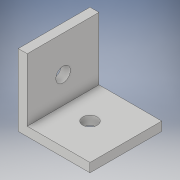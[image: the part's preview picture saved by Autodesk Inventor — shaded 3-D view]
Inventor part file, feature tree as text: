
AUTODESK INVENTOR PART (.ipt)
format: ipt  version: 2018 (Build 220112000, 112)  size: 116,224 bytes
history: native  units: in
note: dims shown in document units (in); Inventor stores cm internally (conversion verified against a paired STEP export)
features: extrude x3, sketch x3
ambient origin geometry x8: Origin, YZ Plane, XZ Plane, XY Plane, X Axis, Y Axis, Z Axis, Center Point
bodies: Solid1 (feature_tree)
feature tree (6):
  extrude  "Extrusion1"  Depth=1.0in
  extrude  "Extrusion2"  Depth=0.125in
  extrude  "Extrusion3"  Depth=1.0in
  sketch  "Sketch1"  dims[d0=0.125in d1=1.0in]
  sketch  "Sketch2"  dims[d2=1.0in d3=0.125in]
  sketch  "Sketch3"  dims[d4=1.0in d5=0.0in d6=0.5in d7=90.0deg d8=0.2031in d9=1.0in d10=0.0in d11=0.5in d12=180.0deg d13=0.2031in d14=1.0in d15=0.0in]
